# Revit family: pk-rp28112lka20_60hz
name_source: partatom
category: 機械設備
units: mm (PartAtom-declared; Revit-internal decimal feet)

## family parameters
OmniClass タイトル = Split System Air Conditioning Units
OmniClass 番号 = 23.75.10.24.21.27.27
パーツ タイプ = 標準
ロード時にボイドで切り取り = いいえ
丸型コネクタ寸法 = 直径を使用
作業面ベース = いいえ
共有 = いいえ
常に垂直 = はい
部屋計算ポイント = はい

## types (9) — shared parameters
Clearance Back = 0 mm
Clearance Bottom = 1800 mm
Clearance Front = 1500 mm
IfcExportAs = IfcUnitaryEquipmentType
IfcExportType = AIRCONDITIONINGUNIT
OmniClassCode = 23-33 17 13 11
Space Bot_1 = 7 mm
Space Bot_2 = 250 mm
URL = https://www.mitsubishielectric.co.jp
Uniclass2015Code = Pr_70_65_03_84
Uniclass2015Title = Split coil remote air cooled condensing units
Uniclass2015Version = Systems v1.9
ケーブルサイズ = 0 mm
サービススペース = はい
サービススペース PK-RP40LA～PK-RP50LA / PK-RP80KA～PK-RP112KA = はい
サービススペース PK-RP56KA～PK-RP71KA = いいえ
ドレン管径 = 16.00 mm
ドレン管径 (外径) = 22 mm
パネルマテリアル = <カテゴリ別>
仕様書バージョン = Version1.0
企業コード = 108420
冷媒管径 = 100.00 mm
冷媒高低圧ガス管径 = 0.00 mm
分類コード = 5.0053E+13
加湿給水管径 = 0.00 mm
参照している仕様書等のバージョン = 公共建築工事標準仕様書（機械設備工事編）平成31年度版
吊りボルト_H = 0 mm
吊り位置X = 0 mm
吊り位置Y = 0 mm
周波数 = 60 Hz
呼称 = 室内機_壁掛（露出）形
壁掛_PK-RP56_71KA17 = いいえ
始動方式 = 直入
形式 = 壁掛（露出）形
推奨ブレーカー容量 = 0 A
本体マテリアル = <カテゴリ別>
極数 = 1
法定耐用年数 = 6
発停方法 = 付属スイッチ
相 = 1
積算_科目 = 1 空気調和設備
符号 = PAC_WR
製品出荷対象 = 国内
製造元 = 三菱電機株式会社
設置方法 = 壁掛形
設計冷房能力 = 0 kW
設計冷房能力_顕熱 = 0 kW
設計暖房能力 = 0.00 kW
説明 = 店舗・事務所用パッケージエアコン(Mr.SLIM) 壁掛形<ワイヤード>
負荷分類 = 3_ファン類
運転質量 = 0.00 kg
電圧 = 0 V
電源_H = 0 mm
zero-valued in all types: 価格, 有効加湿量

## per-type parameters (varying)
- 壁掛_PK-RP28LA4: Clearance Left=50 mm; Clearance Right=150 mm; Clearance Top=50 mm; Depth=237 mm; Height=299 mm; MAX風量=522.0 m³/h; MID風量=480.0 m³/h; MIN風量=438.0 m³/h; S_H=356 mm; Space Left=50 mm; Space Right=150 mm; Space Right_1=260 mm; Space Top=50 mm; Width=898 mm; ドレン位置-X=660 mm; ドレン位置-Y=37 mm; ドレン位置-Z=274 mm; 冷媒ガス管位置-X=642 mm; 冷媒ガス管位置-Y=23 mm; 冷媒ガス管位置-Z=268 mm; 冷媒ガス管径=12.70 mm; 冷媒液管位置-X=711 mm; 冷媒液管位置-Y=23 mm; 冷媒液管位置-Z=280 mm; 冷媒液管径=6.35 mm; 冷媒管径符号=Ac; 冷房能力=2.5 kW; 壁掛_PK-RP40_50LA=はい; 壁掛_PK-RP80_112KA17=いいえ; 暖房能力=2.80 kW; 構成品番=PK-RP28LA4; 消費電力=0.03 kW; 消費電力_冷房=0.03 kW; 消費電力_暖房=0.02 kW; 製品質量=12.50 kg; 質量=15.00 kg; 電動機出力_送風機=0.03 kW; 音響パワーレベル(dB)=52; 音響パワーレベル_中 (dB)=50; 音響パワーレベル_弱 (dB)=48; 音響パワーレベル_強 (dB)=52; 音響パワーレベル_静 (dB)=45; 風量=522.0 m³/h; 風量_中 (m3/min)=8; 風量_弱 (m3/min)=7.3; 風量_強 (m3/min)=8.7; 風量_静 (m3/min)=6.3
- 壁掛_PK-RP40LA4: Clearance Left=50 mm; Clearance Right=150 mm; Clearance Top=50 mm; Depth=237 mm; Height=299 mm; MAX風量=642.0 m³/h; MID風量=564.0 m³/h; MIN風量=492.0 m³/h; S_H=356 mm; Space Left=50 mm; Space Right=150 mm; Space Right_1=260 mm; Space Top=50 mm; Width=898 mm; ドレン位置-X=660 mm; ドレン位置-Y=35 mm; ドレン位置-Z=245 mm; 冷媒ガス管位置-X=642 mm; 冷媒ガス管位置-Y=35 mm; 冷媒ガス管位置-Z=268 mm; 冷媒ガス管径=12.70 mm; 冷媒液管位置-X=711 mm; 冷媒液管位置-Y=35 mm; 冷媒液管位置-Z=280 mm; 冷媒液管径=6.35 mm; 冷媒管径符号=Ac; 冷房能力=3.6 kW; 壁掛_PK-RP40_50LA=はい; 壁掛_PK-RP80_112KA17=いいえ; 暖房能力=4.00 kW; 構成品番=PK-RP40LA4; 消費電力=0.04 kW; 消費電力_冷房=0.04 kW; 消費電力_暖房=0.03 kW; 製品質量=12.50 kg; 質量=15.00 kg; 電動機出力_送風機=0.03 kW; 音響パワーレベル(dB)=57; 音響パワーレベル_中 (dB)=54; 音響パワーレベル_弱 (dB)=51; 音響パワーレベル_強 (dB)=57; 音響パワーレベル_静 (dB)=47; 風量=642.0 m³/h; 風量_中 (m3/min)=9.4; 風量_弱 (m3/min)=8.2; 風量_強 (m3/min)=10.7; 風量_静 (m3/min)=6.8
- 壁掛_PK-RP45LA4: Clearance Left=50 mm; Clearance Right=150 mm; Clearance Top=50 mm; Depth=237 mm; Height=299 mm; MAX風量=642.0 m³/h; MID風量=564.0 m³/h; MIN風量=492.0 m³/h; S_H=356 mm; Space Left=50 mm; Space Right=150 mm; Space Right_1=260 mm; Space Top=50 mm; Width=898 mm; ドレン位置-X=660 mm; ドレン位置-Y=35 mm; ドレン位置-Z=245 mm; 冷媒ガス管位置-X=642 mm; 冷媒ガス管位置-Y=35 mm; 冷媒ガス管位置-Z=268 mm; 冷媒ガス管径=12.70 mm; 冷媒液管位置-X=711 mm; 冷媒液管位置-Y=35 mm; 冷媒液管位置-Z=280 mm; 冷媒液管径=6.35 mm; 冷媒管径符号=Ac; 冷房能力=4 kW; 壁掛_PK-RP40_50LA=はい; 壁掛_PK-RP80_112KA17=いいえ; 暖房能力=4.50 kW; 構成品番=PK-RP45LA4; 消費電力=0.04 kW; 消費電力_冷房=0.04 kW; 消費電力_暖房=0.03 kW; 製品質量=12.50 kg; 質量=15.00 kg; 電動機出力_送風機=0.03 kW; 音響パワーレベル(dB)=57; 音響パワーレベル_中 (dB)=54; 音響パワーレベル_弱 (dB)=51; 音響パワーレベル_強 (dB)=57; 音響パワーレベル_静 (dB)=48; 風量=642.0 m³/h; 風量_中 (m3/min)=9.4; 風量_弱 (m3/min)=8.2; 風量_強 (m3/min)=10.7; 風量_静 (m3/min)=6.8
- 壁掛_PK-RP50LA4: Clearance Left=50 mm; Clearance Right=150 mm; Clearance Top=50 mm; Depth=237 mm; Height=299 mm; MAX風量=642.0 m³/h; MID風量=564.0 m³/h; MIN風量=492.0 m³/h; S_H=356 mm; Space Left=50 mm; Space Right=150 mm; Space Right_1=260 mm; Space Top=50 mm; Width=898 mm; ドレン位置-X=660 mm; ドレン位置-Y=35 mm; ドレン位置-Z=245 mm; 冷媒ガス管位置-X=642 mm; 冷媒ガス管位置-Y=35 mm; 冷媒ガス管位置-Z=268 mm; 冷媒ガス管径=12.70 mm; 冷媒液管位置-X=711 mm; 冷媒液管位置-Y=35 mm; 冷媒液管位置-Z=280 mm; 冷媒液管径=6.35 mm; 冷媒管径符号=Ac; 冷房能力=4.5 kW; 壁掛_PK-RP40_50LA=はい; 壁掛_PK-RP80_112KA17=いいえ; 暖房能力=5.00 kW; 構成品番=PK-RP50LA4; 消費電力=0.04 kW; 消費電力_冷房=0.04 kW; 消費電力_暖房=0.03 kW; 製品質量=12.50 kg; 質量=15.00 kg; 電動機出力_送風機=0.03 kW; 音響パワーレベル(dB)=57; 音響パワーレベル_中 (dB)=54; 音響パワーレベル_弱 (dB)=51; 音響パワーレベル_強 (dB)=57; 音響パワーレベル_静 (dB)=48; 風量=642.0 m³/h; 風量_中 (m3/min)=9.4; 風量_弱 (m3/min)=8.2; 風量_強 (m3/min)=10.7; 風量_静 (m3/min)=6.8
- 壁掛_PK-RP56LA4: Clearance Left=50 mm; Clearance Right=150 mm; Clearance Top=50 mm; Depth=237 mm; Height=299 mm; MAX風量=816.0 m³/h; MID風量=696.0 m³/h; MIN風量=564.0 m³/h; S_H=356 mm; Space Left=50 mm; Space Right=150 mm; Space Right_1=260 mm; Space Top=50 mm; Width=898 mm; ドレン位置-X=660 mm; ドレン位置-Y=35 mm; ドレン位置-Z=245 mm; 冷媒ガス管位置-X=642 mm; 冷媒ガス管位置-Y=35 mm; 冷媒ガス管位置-Z=268 mm; 冷媒ガス管径=12.70 mm; 冷媒液管位置-X=711 mm; 冷媒液管位置-Y=35 mm; 冷媒液管位置-Z=280 mm; 冷媒液管径=6.35 mm; 冷媒管径符号=Ac; 冷房能力=5 kW; 壁掛_PK-RP40_50LA=はい; 壁掛_PK-RP80_112KA17=いいえ; 暖房能力=5.60 kW; 構成品番=PK-RP56LA4; 消費電力=0.06 kW; 消費電力_冷房=0.06 kW; 消費電力_暖房=0.05 kW; 製品質量=12.50 kg; 質量=15.00 kg; 電動機出力_送風機=0.03 kW; 音響パワーレベル(dB)=63; 音響パワーレベル_中 (dB)=59; 音響パワーレベル_弱 (dB)=54; 音響パワーレベル_強 (dB)=63; 音響パワーレベル_静 (dB)=49; 風量=816.0 m³/h; 風量_中 (m3/min)=11.6; 風量_弱 (m3/min)=9.4; 風量_強 (m3/min)=13.6; 風量_静 (m3/min)=7.3
- 壁掛_PK-RP63KA20: Clearance Left=52 mm; Clearance Right=101 mm; Clearance Top=48 mm; Depth=295 mm; Height=365 mm; MAX風量=1140.0 m³/h; MID風量=1068.0 m³/h; MIN風量=990.0 m³/h; S_H=420 mm; Space Left=52 mm; Space Right=101 mm; Space Right_1=220 mm; Space Top=48 mm; Width=1170 mm; ドレン位置-X=719 mm; ドレン位置-Y=61 mm; ドレン位置-Z=347 mm; 冷媒ガス管位置-X=567 mm; 冷媒ガス管位置-Y=25 mm; 冷媒ガス管位置-Z=333 mm; 冷媒ガス管径=12.70 mm; 冷媒液管位置-X=636 mm; 冷媒液管位置-Y=30 mm; 冷媒液管位置-Z=312 mm; 冷媒液管径=6.35 mm; 冷媒管径符号=Ac; 冷房能力=5.6 kW; 壁掛_PK-RP40_50LA=いいえ; 壁掛_PK-RP80_112KA17=はい; 暖房能力=6.30 kW; 構成品番=PK-RP63KA20; 消費電力=0.06 kW; 消費電力_冷房=0.06 kW; 消費電力_暖房=0.06 kW; 製品質量=20.00 kg; 質量=24.00 kg; 電動機出力_送風機=0.06 kW; 音響パワーレベル(dB)=56; 音響パワーレベル_中 (dB)=55; 音響パワーレベル_弱 (dB)=53; 音響パワーレベル_強 (dB)=56; 音響パワーレベル_静 (dB)=0; 風量=1140.0 m³/h; 風量_中 (m3/min)=17.8; 風量_弱 (m3/min)=16.5; 風量_強 (m3/min)=19; 風量_静 (m3/min)=0
- 壁掛_PK-RP71KA20: Clearance Left=52 mm; Clearance Right=101 mm; Clearance Top=48 mm; Depth=295 mm; Height=365 mm; MAX風量=1140.0 m³/h; MID風量=1068.0 m³/h; MIN風量=990.0 m³/h; S_H=420 mm; Space Left=52 mm; Space Right=101 mm; Space Right_1=220 mm; Space Top=48 mm; Width=1170 mm; ドレン位置-X=719 mm; ドレン位置-Y=61 mm; ドレン位置-Z=347 mm; 冷媒ガス管位置-X=567 mm; 冷媒ガス管位置-Y=25 mm; 冷媒ガス管位置-Z=333 mm; 冷媒ガス管径=15.88 mm; 冷媒液管位置-X=636 mm; 冷媒液管位置-Y=30 mm; 冷媒液管位置-Z=312 mm; 冷媒液管径=9.52 mm; 冷媒管径符号=Bd; 冷房能力=6.3 kW; 壁掛_PK-RP40_50LA=いいえ; 壁掛_PK-RP80_112KA17=はい; 暖房能力=7.10 kW; 構成品番=PK-RP71KA20; 消費電力=0.06 kW; 消費電力_冷房=0.06 kW; 消費電力_暖房=0.06 kW; 製品質量=21.00 kg; 質量=25.20 kg; 電動機出力_送風機=0.06 kW; 音響パワーレベル(dB)=56; 音響パワーレベル_中 (dB)=55; 音響パワーレベル_弱 (dB)=53; 音響パワーレベル_強 (dB)=56; 音響パワーレベル_静 (dB)=0; 風量=1140.0 m³/h; 風量_中 (m3/min)=17.8; 風量_弱 (m3/min)=16.5; 風量_強 (m3/min)=19; 風量_静 (m3/min)=0
- 壁掛_PK-RP80KA20: Clearance Left=52 mm; Clearance Right=101 mm; Clearance Top=48 mm; Depth=295 mm; Height=365 mm; MAX風量=1380.0 m³/h; MID風量=1200.0 m³/h; MIN風量=1020.0 m³/h; S_H=420 mm; Space Left=52 mm; Space Right=101 mm; Space Right_1=220 mm; Space Top=48 mm; Width=1170 mm; ドレン位置-X=719 mm; ドレン位置-Y=61 mm; ドレン位置-Z=347 mm; 冷媒ガス管位置-X=567 mm; 冷媒ガス管位置-Y=25 mm; 冷媒ガス管位置-Z=333 mm; 冷媒ガス管径=15.88 mm; 冷媒液管位置-X=636 mm; 冷媒液管位置-Y=30 mm; 冷媒液管位置-Z=312 mm; 冷媒液管径=9.52 mm; 冷媒管径符号=Bd; 冷房能力=7.1 kW; 壁掛_PK-RP40_50LA=いいえ; 壁掛_PK-RP80_112KA17=はい; 暖房能力=8.00 kW; 構成品番=PK-RP80KA20; 消費電力=0.07 kW; 消費電力_冷房=0.07 kW; 消費電力_暖房=0.07 kW; 製品質量=21.00 kg; 質量=25.20 kg; 電動機出力_送風機=0.06 kW; 音響パワーレベル(dB)=61; 音響パワーレベル_中 (dB)=57; 音響パワーレベル_弱 (dB)=53; 音響パワーレベル_強 (dB)=61; 音響パワーレベル_静 (dB)=0; 風量=1380.0 m³/h; 風量_中 (m3/min)=20; 風量_弱 (m3/min)=17; 風量_強 (m3/min)=23; 風量_静 (m3/min)=0
- 壁掛_PK-RP112KA20: Clearance Left=52 mm; Clearance Right=101 mm; Clearance Top=48 mm; Depth=295 mm; Height=365 mm; MAX風量=1500.0 m³/h; MID風量=1260.0 m³/h; MIN風量=1020.0 m³/h; S_H=420 mm; Space Left=52 mm; Space Right=101 mm; Space Right_1=220 mm; Space Top=48 mm; Width=1170 mm; ドレン位置-X=719 mm; ドレン位置-Y=61 mm; ドレン位置-Z=347 mm; 冷媒ガス管位置-X=567 mm; 冷媒ガス管位置-Y=25 mm; 冷媒ガス管位置-Z=333 mm; 冷媒ガス管径=15.88 mm; 冷媒液管位置-X=636 mm; 冷媒液管位置-Y=30 mm; 冷媒液管位置-Z=312 mm; 冷媒液管径=9.52 mm; 冷媒管径符号=Bd; 冷房能力=10 kW; 壁掛_PK-RP40_50LA=いいえ; 壁掛_PK-RP80_112KA17=はい; 暖房能力=11.20 kW; 構成品番=PK-RP112KA20; 消費電力=0.07 kW; 消費電力_冷房=0.07 kW; 消費電力_暖房=0.07 kW; 製品質量=21.00 kg; 質量=25.20 kg; 電動機出力_送風機=0.06 kW; 音響パワーレベル(dB)=66; 音響パワーレベル_中 (dB)=61; 音響パワーレベル_弱 (dB)=56; 音響パワーレベル_強 (dB)=66; 音響パワーレベル_静 (dB)=0; 風量=1500.0 m³/h; 風量_中 (m3/min)=21; 風量_弱 (m3/min)=17; 風量_強 (m3/min)=25; 風量_静 (m3/min)=0

## geometry (parser evidence)
native form markers: Sweep x1
no freeform markers — native parametric forms only
